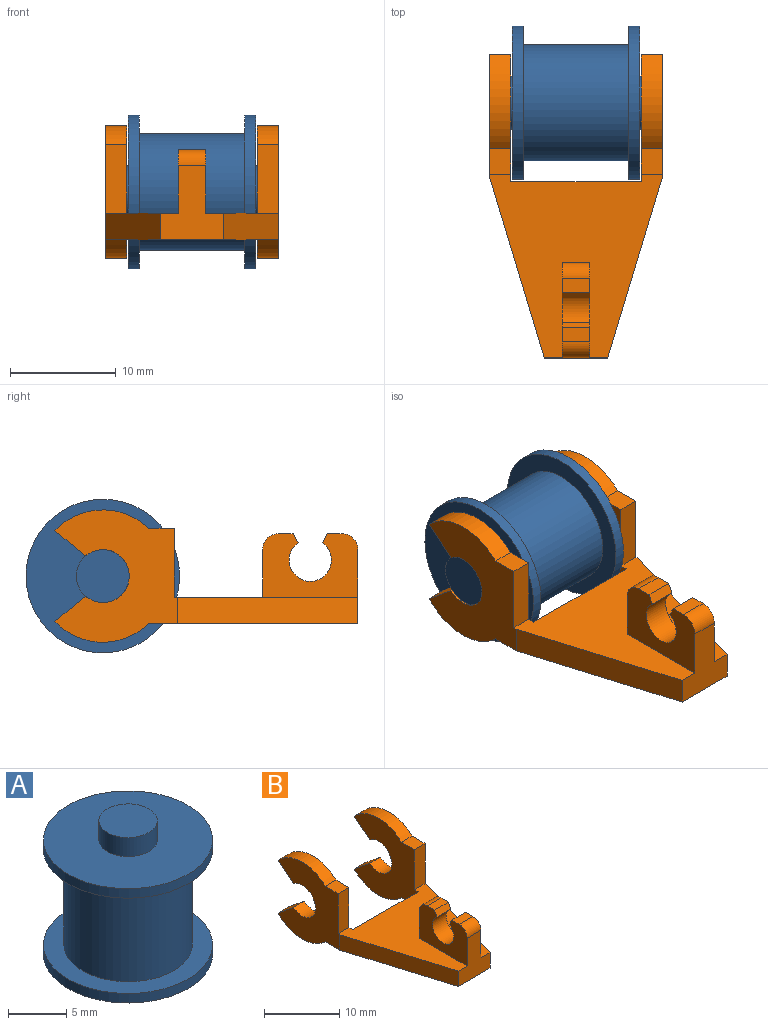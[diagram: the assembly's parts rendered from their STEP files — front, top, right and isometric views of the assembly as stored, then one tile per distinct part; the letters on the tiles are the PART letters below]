
ASSEMBLY  parts=2 mates=1
PART A: 11 faces, bbox 14.5x14.5x16 mm
  f0: cylinder r=7.25mm len=14.5mm, axis (0,0,-1), area 45.6mm2, adj f1,f2
  f1: plane 14.5x14.5mm, normal (0,0,1), area 70.1mm2, adj f0,f3
  f2: plane 14.5x14.5mm, normal (0,0,-1), area 145.5mm2, adj f0,f4
  f3: cylinder r=5.5mm len=11mm, axis (0,0,-1), area 345.6mm2, adj f1,f7
  f4: cylinder r=2.5mm len=5mm, axis (0,0,1), area 31.4mm2, adj f2,f5
  f5: plane 5x5mm, normal (0,0,-1), area 19.6mm2, adj f4
  f6: cylinder r=7.25mm len=14.5mm, axis (0,0,1), area 45.6mm2, adj f7,f8
  f7: plane 14.5x14.5mm, normal (0,0,-1), area 70.1mm2, adj f3,f6
  f8: plane 14.5x14.5mm, normal (0,0,1), area 145.5mm2, adj f6,f9
  f9: cylinder r=2.5mm len=5mm, axis (0,0,-1), area 31.4mm2, adj f8,f10
  f10: plane 5x5mm, normal (0,0,1), area 19.6mm2, adj f9
PART B: 34 faces, bbox 16.3x28.6x12.5 mm
  f0: plane 17.33x16.3mm, normal (0,0,1), area 163mm2, adj f3,f4,f5,f6,f7,f8,f9,f10
  f1: plane 2.42x2mm, normal (0,0,1), area 4.8mm2, adj f3,f9,f14,f22
  f2: plane 2.42x2mm, normal (0,0,1), area 4.8mm2, adj f7,f10,f19,f23
  f3: plane 12.5x11.63mm, normal (-1,0,0), area 88mm2, adj f0,f1,f4,f11,f12,f13,f14,f15
  f4: plane 17x5.15mm, normal (-0.96,-0.29,0), area 44.4mm2, adj f0,f3,f5,f11
  f5: plane 7x6mm, normal (0,-1,0), area 26.7mm2, adj f0,f4,f6,f11,f30,f31,f32
  f6: plane 17x5.15mm, normal (0.96,-0.29,0), area 44.4mm2, adj f0,f5,f7,f11
  f7: plane 12.5x11.63mm, normal (1,0,0), area 88mm2, adj f0,f2,f6,f11,f17,f18,f19,f20
  f8: plane 12.3x2.5mm, normal (0,1,0), area 30.7mm2, adj f0,f9,f10,f11
  f9: plane 12.5x12mm, normal (1,0,0), area 88.9mm2, adj f0,f1,f8,f11,f12,f13,f14,f15
  f10: plane 12.5x12mm, normal (-1,0,0), area 88.9mm2, adj f0,f2,f8,f11,f17,f18,f19,f20
  f11: plane 19.75x16.3mm, normal (0,0,-1), area 196mm2, adj f3,f4,f5,f6,f7,f8,f9,f10
  f12: cylinder r=6.25mm len=8.88mm, axis (-1,0,0), area 19.8mm2, adj f3,f9,f11,f15
  f13: plane 2.92x2.39mm, normal (0,0.63,-0.77), area 7.5mm2, adj f3,f9,f14,f16
  f14: cylinder r=6.25mm len=8.88mm, axis (-1,0,0), area 19.8mm2, adj f1,f3,f9,f13
  f15: plane 2.92x2.39mm, normal (0,0.63,0.77), area 7.5mm2, adj f3,f9,f12,f16
  f16: cylinder r=2.5mm len=5mm, axis (-1,0,0), area 22.8mm2, adj f3,f9,f13,f15
  f17: cylinder r=6.25mm len=8.88mm, axis (-1,0,0), area 19.8mm2, adj f7,f10,f11,f20
  f18: plane 2.92x2.39mm, normal (0,0.63,-0.77), area 7.5mm2, adj f7,f10,f19,f21
  f19: cylinder r=6.25mm len=8.88mm, axis (-1,0,0), area 19.8mm2, adj f2,f7,f10,f18
  f20: plane 2.92x2.39mm, normal (0,0.63,0.77), area 7.5mm2, adj f7,f10,f17,f21
  f21: cylinder r=2.5mm len=5mm, axis (-1,0,0), area 22.8mm2, adj f7,f10,f18,f20
  f22: plane 6.5x2mm, normal (0,-1,0), area 13mm2, adj f0,f1,f3,f9
  f23: plane 6.5x2mm, normal (0,-1,0), area 13mm2, adj f0,f2,f7,f10
  f24: plane 2.6x1.37mm, normal (0,0,1), area 3.6mm2, adj f29,f30,f31,f32
  f25: plane 4.5x2.6mm, normal (0,1,0), area 11.7mm2, adj f0,f30,f31,f33
  f26: plane 2.6x1.37mm, normal (0,0,1), area 3.6mm2, adj f27,f30,f31,f33
  f27: plane 2.6x0.87mm, normal (0,-0.88,0.48), area 2.6mm2, adj f26,f28,f30,f31
  f28: cylinder r=2mm len=4mm, axis (-1,0,0), area 26.3mm2, adj f27,f29,f30,f31
  f29: plane 2.6x0.87mm, normal (0,0.88,0.48), area 2.6mm2, adj f24,f28,f30,f31
  f30: plane 9x6mm, normal (1,0,0), area 38.6mm2, adj f0,f5,f24,f25,f26,f27,f28,f29
  f31: plane 9x6mm, normal (-1,0,0), area 38.6mm2, adj f0,f5,f24,f25,f26,f27,f28,f29
  f32: cylinder r=1.5mm len=2.6mm, axis (-1,0,0), area 6.1mm2, adj f5,f24,f30,f31
  f33: cylinder r=1.5mm len=2.6mm, axis (1,0,0), area 6.1mm2, adj f25,f26,f30,f31
PLACE A rot(axis=(0,-1,0),90deg) t=(1.69,13.5,7.54)mm
PLACE B t=(-4.31,-3.72,3.04)mm
MATE fastened A.f4 <-> B.f12  axis (1,0,0) through (3.69,13.5,7.54)mm
